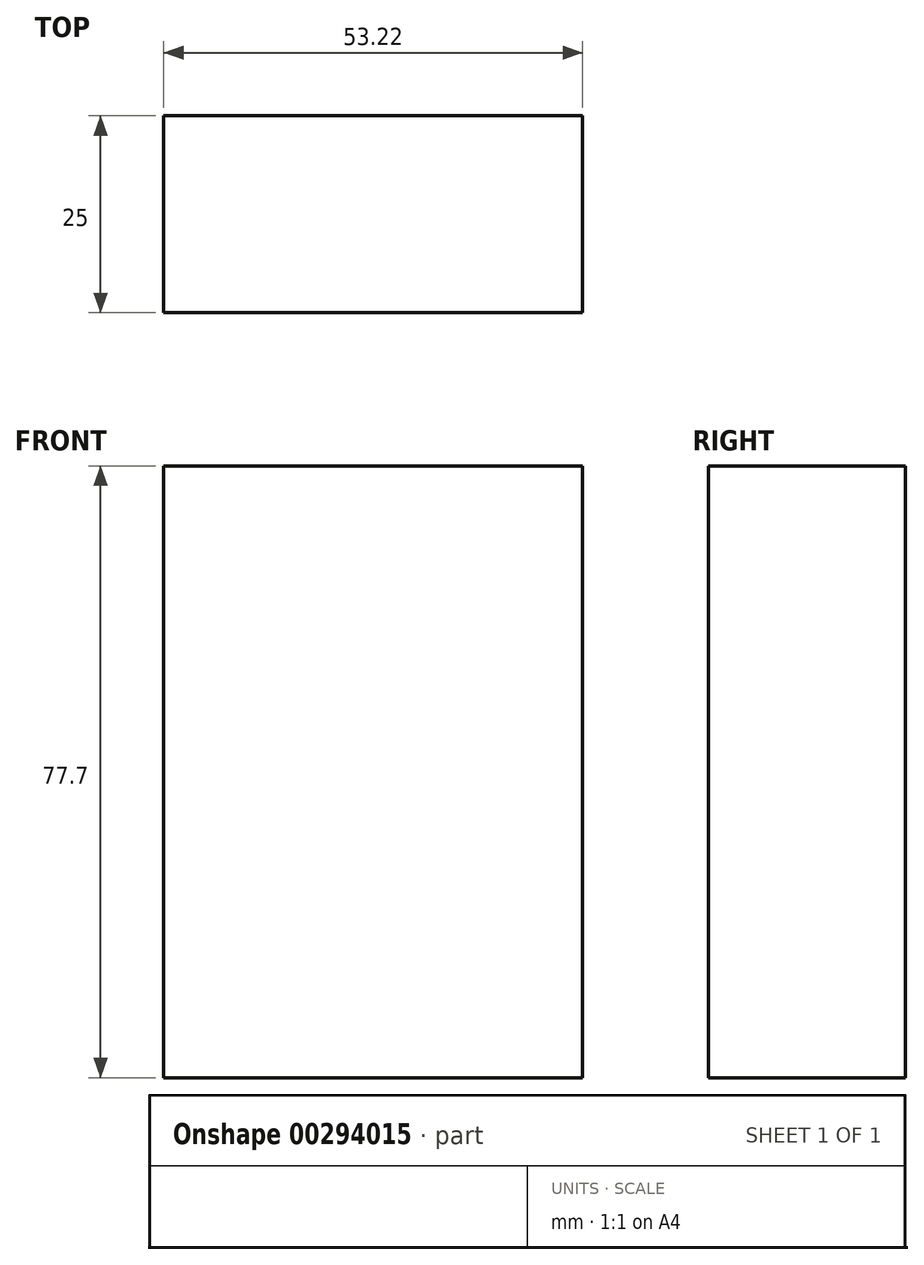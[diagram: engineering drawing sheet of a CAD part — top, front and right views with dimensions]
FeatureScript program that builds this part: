
annotation { "Feature Type Name" : "Feature", "Feature Type Description" : "" }
export const myFeature = defineFeature(function(context is Context, id is Id, definition is map)
    precondition{}
    {
        {
            var Q0;
            Q0=qCreatedBy(makeId("Front.planeOp"),FACE);
            var sketch = newSketch(context, id + "F0", { "sketchPlane" : qUnion([Q0])});
            skLineSegment(sketch, "E0.bottom", {"start": v(-89.9, 0) * mm, "end": v(-36.68, 0) * mm});
            skLineSegment(sketch, "E0.top", {"start": v(-89.9, 77.7) * mm, "end": v(-36.68, 77.7) * mm});
            skLineSegment(sketch, "E0.left", {"start": v(-89.9, 0) * mm, "end": v(-89.9, 77.7) * mm});
            skLineSegment(sketch, "E0.right", {"start": v(-36.68, 0) * mm, "end": v(-36.68, 77.7) * mm});
            skPoint(sketch, "E0.middle", {"position": v(-63.29, 38.85) * mm});
            skSolve(sketch);
        }
        {
            var Q0;
            Q0=makeQuery(id+"F0.imprint","IMPRINT",FACE,{"disambiguationData":[TD([[makeQuery(id+"F0.imprint","IMPRINT",EDGE,{"derivedFrom":sQuery(id+"F0.wireOp",EDGE,"E0.bottom")}),1.0]])]});
            extrude(context, id + "F1", {"entities" : qUnion([Q0]), "depth" : 25 * mm});
        }
    });
